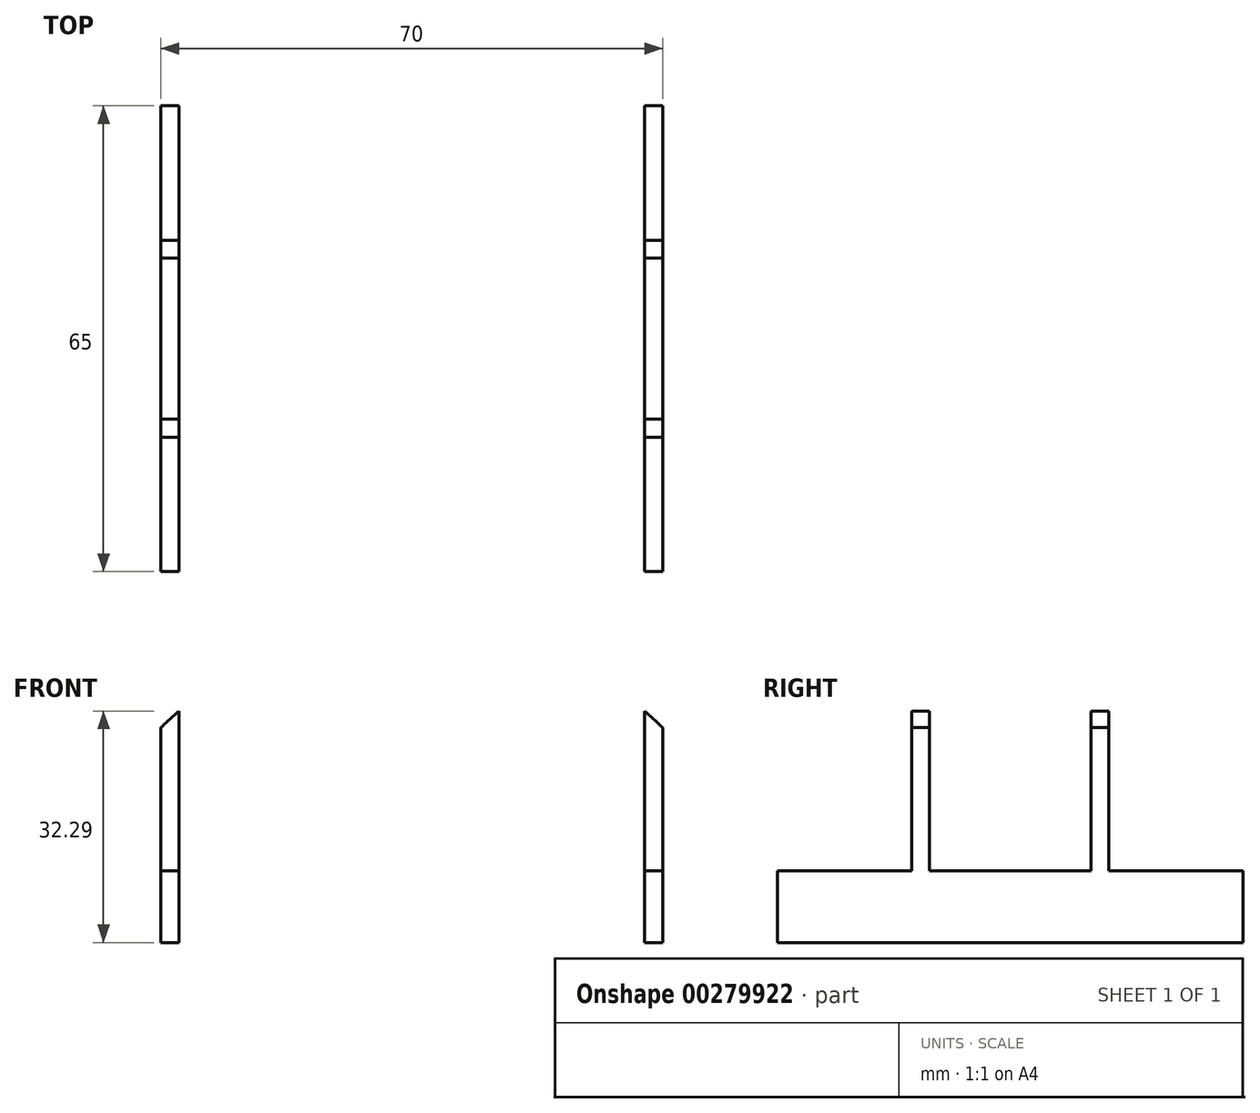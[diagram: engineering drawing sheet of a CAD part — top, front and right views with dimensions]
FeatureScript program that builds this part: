
annotation { "Feature Type Name" : "Feature", "Feature Type Description" : "" }
export const myFeature = defineFeature(function(context is Context, id is Id, definition is map)
    precondition{}
    {
        {
            var Q0;
            Q0=qCreatedBy(makeId("Front.planeOp"),FACE);
            var sketch = newSketch(context, id + "F0", { "sketchPlane" : qUnion([Q0])});
            skArc(sketch, "E0", {"start": v(70, 0) * mm, "mid": v(35, 14.3) * mm, "end": v(0, 0) * mm});
            skLineSegment(sketch, "E1", {"start": v(70, 0) * mm, "end": v(70, -5) * mm});
            skLineSegment(sketch, "E2", {"start": v(0, 0) * mm, "end": v(0, -5) * mm});
            skArc(sketch, "E3", {"start": v(70, -5) * mm, "mid": v(35, 9.3) * mm, "end": v(0, -5) * mm});
            skSolve(sketch);
        }
        {
            var Q0;
            Q0 = qSketchRegion(id + "F0", true);
            extrude(context, id + "F1", {"entities" : qUnion([Q0]), "depth" : 50 * mm});
        }
        {
            var Q0;
            Q0=makeQuery(id+"F1.opExtrude","SWEPT_FACE",FACE,{"disambiguationData":[OSD([sQuery(id+"F0.wireOp",EDGE,"E1")])]});
            var sketch = newSketch(context, id + "F2", { "sketchPlane" : qUnion([Q0])});
            skLineSegment(sketch, "E4", {"start": v(-25, -5) * mm, "end": v(-25, 0) * mm});
            skLineSegment(sketch, "E5", {"start": v(-38.75, -5) * mm, "end": v(-38.75, -30) * mm});
            skLineSegment(sketch, "E6", {"start": v(-38.75, -30) * mm, "end": v(-36.25, -30) * mm});
            skLineSegment(sketch, "E7", {"start": v(-36.25, -30) * mm, "end": v(-36.25, -5) * mm});
            skLineSegment(sketch, "E8", {"start": v(-36.25, -5) * mm, "end": v(-36.25, -2.5) * mm});
            skLineSegment(sketch, "E9", {"start": v(-36.25, -2.5) * mm, "end": v(-38.75, -2.5) * mm});
            skLineSegment(sketch, "E10", {"start": v(-38.75, -2.5) * mm, "end": v(-38.75, -5) * mm});
            skLineSegment(sketch, "E11", {"start": v(-11.25, -5) * mm, "end": v(-11.25, -30) * mm});
            skLineSegment(sketch, "E12", {"start": v(-11.25, -30) * mm, "end": v(-13.75, -30) * mm});
            skLineSegment(sketch, "E13", {"start": v(-13.75, -30) * mm, "end": v(-13.75, -5) * mm});
            skLineSegment(sketch, "E14", {"start": v(-13.75, -5) * mm, "end": v(-13.75, -2.5) * mm});
            skLineSegment(sketch, "E15", {"start": v(-13.75, -2.5) * mm, "end": v(-11.25, -2.5) * mm});
            skLineSegment(sketch, "E16", {"start": v(-11.25, -2.5) * mm, "end": v(-11.25, -5) * mm});
            skCircle(sketch, "E17", {"center": v(-37.5, -2.5) * mm, "radius": 1.25 * mm});
            skCircle(sketch, "E18", {"center": v(-12.5, -2.5) * mm, "radius": 1.25 * mm});
            skLineSegment(sketch, "E19", {"start": v(-57.5, -30) * mm, "end": v(-57.5, -25) * mm});
            skLineSegment(sketch, "E20", {"start": v(7.5, -30) * mm, "end": v(7.5, -35) * mm});
            skLineSegment(sketch, "E21.bottom", {"start": v(-57.5, -25) * mm, "end": v(7.5, -25) * mm});
            skLineSegment(sketch, "E21.top", {"start": v(-57.5, -35) * mm, "end": v(7.5, -35) * mm});
            skLineSegment(sketch, "E21.left", {"start": v(-57.5, -25) * mm, "end": v(-57.5, -35) * mm});
            skLineSegment(sketch, "E21.right", {"start": v(7.5, -25) * mm, "end": v(7.5, -35) * mm});
            skSolve(sketch);
        }
        {
            var Q0;
            Q0 = qSketchRegion(id + "F2", true);
            extrude(context, id + "F3", {"entities" : qUnion([Q0]), "operationType" : NewBodyOperationType.ADD, "oppositeDirection" : true, "depth" : 2.5 * mm});
        }
        {
            var Q0;
            Q0=makeQuery(id+"F1.opExtrude","SWEPT_FACE",FACE,{"disambiguationData":[OSD([sQuery(id+"F0.wireOp",EDGE,"E2")])]});
            var sketch = newSketch(context, id + "F4", { "sketchPlane" : qUnion([Q0])});
            skLineSegment(sketch, "E22", {"start": v(12.5, -5) * mm, "end": v(11.25, -5) * mm});
            skLineSegment(sketch, "E23", {"start": v(11.25, -5) * mm, "end": v(11.25, -30) * mm});
            skLineSegment(sketch, "E24", {"start": v(11.25, -30) * mm, "end": v(13.75, -30) * mm});
            skLineSegment(sketch, "E25", {"start": v(13.75, -30) * mm, "end": v(13.75, -5) * mm});
            skLineSegment(sketch, "E26", {"start": v(13.75, -5) * mm, "end": v(13.75, -2.5) * mm});
            skLineSegment(sketch, "E27", {"start": v(13.75, -2.5) * mm, "end": v(11.25, -2.5) * mm});
            skLineSegment(sketch, "E28", {"start": v(11.25, -2.5) * mm, "end": v(11.25, -5) * mm});
            skLineSegment(sketch, "E29", {"start": v(37.5, -5) * mm, "end": v(36.25, -5) * mm});
            skLineSegment(sketch, "E30", {"start": v(36.25, -5) * mm, "end": v(36.25, -30) * mm});
            skLineSegment(sketch, "E31", {"start": v(36.25, -30) * mm, "end": v(38.75, -30) * mm});
            skLineSegment(sketch, "E32", {"start": v(38.75, -30) * mm, "end": v(38.75, -2.5) * mm});
            skLineSegment(sketch, "E33", {"start": v(38.75, -2.5) * mm, "end": v(36.25, -2.5) * mm});
            skLineSegment(sketch, "E34", {"start": v(36.25, -2.5) * mm, "end": v(36.25, -5) * mm});
            skCircle(sketch, "E35", {"center": v(12.5, -2.5) * mm, "radius": 1.25 * mm});
            skCircle(sketch, "E36", {"center": v(37.5, -2.5) * mm, "radius": 1.25 * mm});
            skLineSegment(sketch, "E37", {"start": v(-7.5, -30) * mm, "end": v(-7.5, -25) * mm});
            skLineSegment(sketch, "E38", {"start": v(57.5, -30) * mm, "end": v(57.5, -35) * mm});
            skLineSegment(sketch, "E39.bottom", {"start": v(57.5, -35) * mm, "end": v(-7.5, -35) * mm});
            skLineSegment(sketch, "E39.top", {"start": v(57.5, -25) * mm, "end": v(-7.5, -25) * mm});
            skLineSegment(sketch, "E39.left", {"start": v(57.5, -35) * mm, "end": v(57.5, -25) * mm});
            skLineSegment(sketch, "E39.right", {"start": v(-7.5, -35) * mm, "end": v(-7.5, -25) * mm});
            skSolve(sketch);
        }
        {
            var Q0;
            Q0 = qSketchRegion(id + "F4", true);
            extrude(context, id + "F5", {"entities" : qUnion([Q0]), "operationType" : NewBodyOperationType.ADD, "oppositeDirection" : true, "depth" : 2.5 * mm});
        }
        {
            var Q0;
            Q0=makeQuery(id+"F1.opExtrude","CAP_FACE",FACE,{"disambiguationData":[OSD([sQuery(id+"F0.wireOp",EDGE,"E0"),sQuery(id+"F0.wireOp",EDGE,"E1"),sQuery(id+"F0.wireOp",EDGE,"E2"),sQuery(id+"F0.wireOp",EDGE,"E3")])],"isStart":false});
            var sketch = newSketch(context, id + "F6", { "sketchPlane" : qUnion([Q0])});
            skPoint(sketch, "E40.startSnap0", {"position": v(0, -2.5) * mm});
            skArc(sketch, "E41.0.0", {"start": v(0, -5) * mm, "mid": v(35, 9.3) * mm, "end": v(70, -5) * mm});
            skLineSegment(sketch, "E41.0.1", {"start": v(70, -5) * mm, "end": v(70, 0) * mm});
            skArc(sketch, "E41.0.2", {"start": v(70, 0) * mm, "mid": v(35, 14.3) * mm, "end": v(0, 0) * mm});
            skLineSegment(sketch, "E41.0.3", {"start": v(0, 0) * mm, "end": v(0, -5) * mm});
            skLineSegment(sketch, "E42.0.0", {"start": v(70, -25) * mm, "end": v(70, -5) * mm});
            skArc(sketch, "E42.0.1", {"start": v(70, -5) * mm, "mid": v(68.77, -3.83) * mm, "end": v(67.5, -2.71) * mm});
            skLineSegment(sketch, "E42.0.2", {"start": v(67.5, -2.71) * mm, "end": v(67.5, -25) * mm});
            skLineSegment(sketch, "E42.0.3", {"start": v(67.5, -25) * mm, "end": v(70, -25) * mm});
            skLineSegment(sketch, "E43.left", {"start": v(70, 0) * mm, "end": v(70, 0) * mm});
            skLineSegment(sketch, "E43.right", {"start": v(64.03, 0) * mm, "end": v(64.03, 0) * mm});
            skLineSegment(sketch, "E44.top", {"start": v(70, 5) * mm, "end": v(70, 5) * mm});
            skLineSegment(sketch, "E44.left", {"start": v(70, 0) * mm, "end": v(70, 5) * mm});
            skLineSegment(sketch, "E44.right", {"start": v(70, 0) * mm, "end": v(70, 5) * mm});
            skLineSegment(sketch, "E45.bottom", {"start": v(70, 5) * mm, "end": v(64.03, 5) * mm});
            skLineSegment(sketch, "E45.top", {"start": v(70, 5) * mm, "end": v(64.03, 5) * mm});
            skLineSegment(sketch, "E45.right", {"start": v(64.03, 5) * mm, "end": v(64.03, 5) * mm});
            skLineSegment(sketch, "E46", {"start": v(0, 0) * mm, "end": v(0, 5) * mm});
            skLineSegment(sketch, "E47", {"start": v(0, 5) * mm, "end": v(5.97, 5) * mm});
            skLineSegment(sketch, "E48.0.0", {"start": v(2.5, -25) * mm, "end": v(2.5, -2.71) * mm});
            skArc(sketch, "E48.0.1", {"start": v(2.5, -2.71) * mm, "mid": v(1.23, -3.83) * mm, "end": v(0, -5) * mm});
            skLineSegment(sketch, "E48.0.2", {"start": v(0, -5) * mm, "end": v(0, -25) * mm});
            skLineSegment(sketch, "E48.0.3", {"start": v(0, -25) * mm, "end": v(2.5, -25) * mm});
            skLineSegment(sketch, "E49", {"start": v(5.97, 5) * mm, "end": v(2.5, -2.71) * mm});
            skLineSegment(sketch, "E50", {"start": v(67.5, -2.71) * mm, "end": v(64.03, 5) * mm});
            skSolve(sketch);
        }
        {
            var Q0;
            Q0=makeQuery(id+"F6.imprint","IMPRINT",FACE,{"disambiguationData":[TD([[makeQuery(id+"F6.imprint","IMPRINT",EDGE,{"derivedFrom":sQuery(id+"F6.wireOp",EDGE,"E41.0.0")}),-1.0]])]});
            extrude(context, id + "F7", {"entities" : qUnion([Q0]), "operationType" : NewBodyOperationType.REMOVE, "oppositeDirection" : true, "depth" : 50 * mm});
        }
    });
